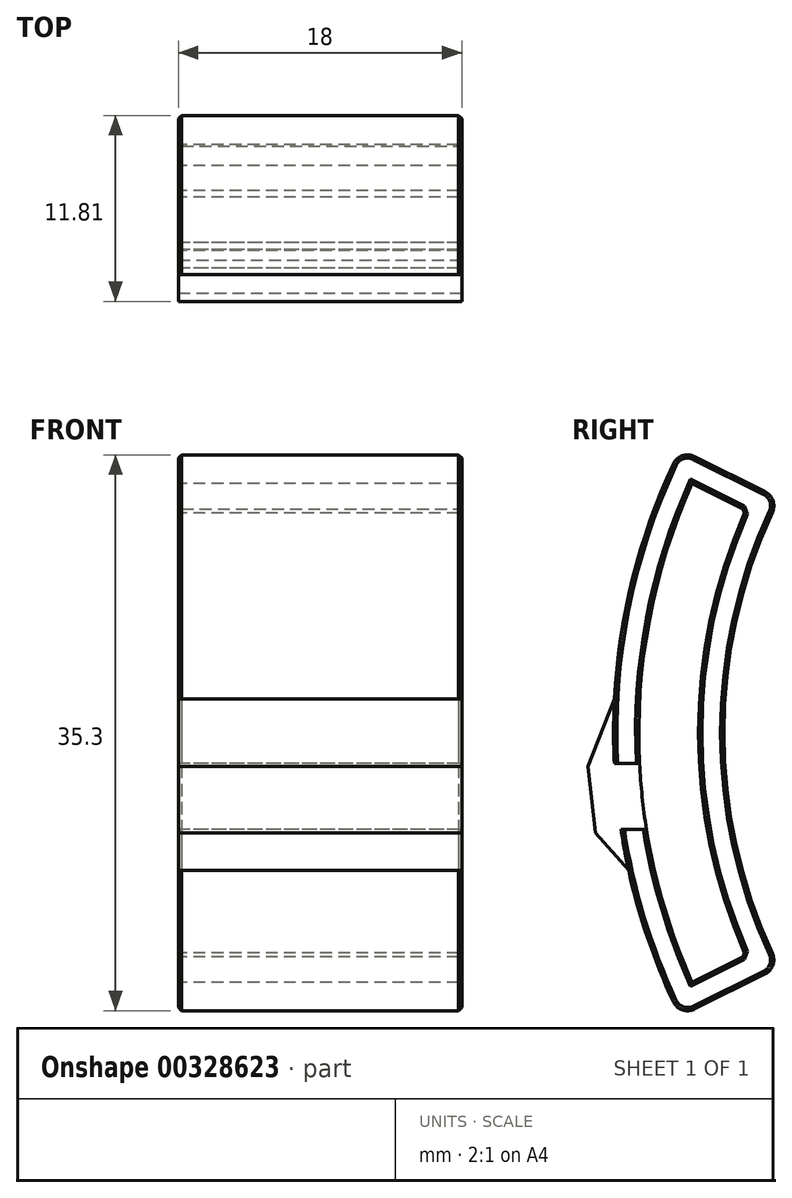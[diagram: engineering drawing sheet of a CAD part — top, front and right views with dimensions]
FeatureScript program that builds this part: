
annotation { "Feature Type Name" : "Feature", "Feature Type Description" : "" }
export const myFeature = defineFeature(function(context is Context, id is Id, definition is map)
    precondition{}
    {
        {
            var Q0;
            Q0=qCreatedBy(makeId("Right.planeOp"),FACE);
            var sketch = newSketch(context, id + "F0", { "sketchPlane" : qUnion([Q0])});
            skLineSegment(sketch, "E0", {"start": v(-58.85, 0) * mm, "end": v(-31.73, 0) * mm, "construction": true});
            skLineSegment(sketch, "E1", {"start": v(-53.7, 17.55) * mm, "end": v(-49.23, 15.32) * mm});
            skArc(sketch, "E2", {"start": v(-55.06, 17.08) * mm, "mid": v(-57.9, 8.75) * mm, "end": v(-58.85, 0) * mm});
            skLineSegment(sketch, "E3", {"start": v(-54.62, 18) * mm, "end": v(-58.85, 9.5) * mm, "construction": true});
            skLineSegment(sketch, "E4", {"start": v(-58.85, 9.5) * mm, "end": v(-58.85, 0) * mm, "construction": true});
            skLineSegment(sketch, "E5", {"start": v(-48.35, 14.88) * mm, "end": v(-51.85, 7.85) * mm, "construction": true});
            skLineSegment(sketch, "E6", {"start": v(-51.85, 7.85) * mm, "end": v(-51.85, 0) * mm, "construction": true});
            skArc(sketch, "E7", {"start": v(-48.77, 14) * mm, "mid": v(-51.07, 7.17) * mm, "end": v(-51.85, 0) * mm});
            skPoint(sketch, "E8.visualSharp", {"position": v(-54.62, 18) * mm});
            skArc(sketch, "E8.filletArc", {"start": v(-53.7, 17.55) * mm, "mid": v(-54.48, 17.6) * mm, "end": v(-55.06, 17.08) * mm});
            skPoint(sketch, "E9.visualSharp", {"position": v(-48.35, 14.88) * mm});
            skArc(sketch, "E9.filletArc", {"start": v(-48.77, 14) * mm, "mid": v(-48.73, 14.75) * mm, "end": v(-49.23, 15.32) * mm});
            skArc(sketch, "E10.0", {"start": v(-53.87, 15.84) * mm, "mid": v(-56.4, 8.1) * mm, "end": v(-57.25, 0) * mm});
            skLineSegment(sketch, "E10.1", {"start": v(-53.87, 15.84) * mm, "end": v(-50.46, 14.14) * mm});
            skArc(sketch, "E10.2", {"start": v(-50.46, 14.14) * mm, "mid": v(-52.7, 7.23) * mm, "end": v(-53.45, 0) * mm});
            skArc(sketch, "E11.MirrorCS", {"start": v(-53.87, -15.84) * mm, "mid": v(-56.4, -8.1) * mm, "end": v(-57.25, 0) * mm});
            skLineSegment(sketch, "E12.MirrorCS", {"start": v(-53.87, -15.84) * mm, "end": v(-50.46, -14.14) * mm});
            skArc(sketch, "E13.MirrorCS", {"start": v(-50.46, -14.14) * mm, "mid": v(-52.7, -7.23) * mm, "end": v(-53.45, 0) * mm});
            skArc(sketch, "E14.MirrorCS", {"start": v(-48.77, -14) * mm, "mid": v(-51.07, -7.17) * mm, "end": v(-51.85, 0) * mm});
            skArc(sketch, "E15.MirrorCS", {"start": v(-48.77, -14) * mm, "mid": v(-48.73, -14.75) * mm, "end": v(-49.23, -15.32) * mm});
            skLineSegment(sketch, "E16.MirrorCS", {"start": v(-53.7, -17.55) * mm, "end": v(-49.23, -15.32) * mm});
            skArc(sketch, "E17.MirrorCS", {"start": v(-53.7, -17.55) * mm, "mid": v(-54.48, -17.6) * mm, "end": v(-55.06, -17.08) * mm});
            skArc(sketch, "E18.MirrorCS", {"start": v(-55.06, -17.08) * mm, "mid": v(-57.9, -8.75) * mm, "end": v(-58.85, 0) * mm});
            skLineSegment(sketch, "E19", {"start": v(-58.8, -1.94) * mm, "end": v(-57.2, -1.94) * mm});
            skLineSegment(sketch, "E20", {"start": v(-58.38, -6.15) * mm, "end": v(-56.76, -6.15) * mm});
            skLineSegment(sketch, "E21", {"start": v(-58.8, 2.15) * mm, "end": v(-60.49, -2.14) * mm});
            skLineSegment(sketch, "E22", {"start": v(-60.49, -2.14) * mm, "end": v(-60, -6.37) * mm});
            skLineSegment(sketch, "E23", {"start": v(-60, -6.37) * mm, "end": v(-57.9, -8.75) * mm});
            skSolve(sketch);
        }
        {
            var Q0;
            Q0=makeQuery(id+"F0.imprint","IMPRINT",FACE,{"disambiguationData":[TD([[makeQuery(id+"F0.imprint","IMPRINT",EDGE,{"derivedFrom":sQuery(id+"F0.wireOp",EDGE,"E1")}),-1.0]])]});
            extrude(context, id + "F1", {"entities" : qUnion([Q0]), "depth" : 18 * mm});
        }
        {
            var Q0;
            Q0=makeQuery(id+"F1.opExtrude","CAP_EDGE",EDGE,{"disambiguationData":[OSD([sQuery(id+"F0.wireOp",EDGE,"E18.MirrorCS")])],"isStart":false});
            var Q1;
            Q1=makeQuery(id+"F1.opExtrude","SWEPT_FACE",FACE,{"disambiguationData":[OSD([sQuery(id+"F0.wireOp",EDGE,"E10.2"),sQuery(id+"F0.wireOp",EDGE,"E13.MirrorCS")])]});
            var Q2;
            Q2=makeQuery(id+"F1.opExtrude","CAP_EDGE",EDGE,{"disambiguationData":[OSD([sQuery(id+"F0.wireOp",EDGE,"E11.MirrorCS")])],"isStart":false});
            var Q3;
            Q3=makeQuery(id+"F1.opExtrude","CAP_EDGE",EDGE,{"disambiguationData":[OSD([sQuery(id+"F0.wireOp",EDGE,"E10.0"),sQuery(id+"F0.wireOp",EDGE,"E11.MirrorCS")])],"isStart":false});
            var Q4;
            Q4=makeQuery(id+"F1.opExtrude","CAP_EDGE",EDGE,{"disambiguationData":[OSD([sQuery(id+"F0.wireOp",EDGE,"E2"),sQuery(id+"F0.wireOp",EDGE,"E18.MirrorCS")])],"isStart":true});
            var Q5;
            Q5=makeQuery(id+"F1.opExtrude","CAP_EDGE",EDGE,{"disambiguationData":[OSD([sQuery(id+"F0.wireOp",EDGE,"E18.MirrorCS")])],"isStart":true});
            var Q6;
            Q6=makeQuery(id+"F1.opExtrude","CAP_EDGE",EDGE,{"disambiguationData":[OSD([sQuery(id+"F0.wireOp",EDGE,"E11.MirrorCS")])],"isStart":true});
            var Q7;
            Q7=makeQuery(id+"F1.opExtrude","CAP_EDGE",EDGE,{"disambiguationData":[OSD([sQuery(id+"F0.wireOp",EDGE,"E10.0"),sQuery(id+"F0.wireOp",EDGE,"E11.MirrorCS")])],"isStart":true});
            chamfer(context, id + "F2", {"entities" : qUnion([Q0, Q1, Q2, Q3, Q4, Q5, Q6, Q7]), "width" : 0.2 * mm, "tangentPropagation" : true});
        }
        {
            var Q0;
            {var subQ6=sQuery(id+"F0.wireOp",EDGE,"E21");Q0=makeQuery(id+"F0.imprint","IMPRINT",FACE,{"disambiguationData":[TD([[makeQuery(id+"F0.imprint","IMPRINT",EDGE,{"derivedFrom":subQ6}),1.0]])]});}
            var Q1;
            {var subQ0=sQuery(id+"F0.wireOp",EDGE,"E19");Q1=makeQuery(id+"F0.imprint","IMPRINT",FACE,{"disambiguationData":[TD([[makeQuery(id+"F0.imprint","IMPRINT",EDGE,{"derivedFrom":subQ0}),-1.0]])]});}
            extrude(context, id + "F3", {"entities" : qUnion([Q0, Q1]), "depth" : 18 * mm});
        }
    });
